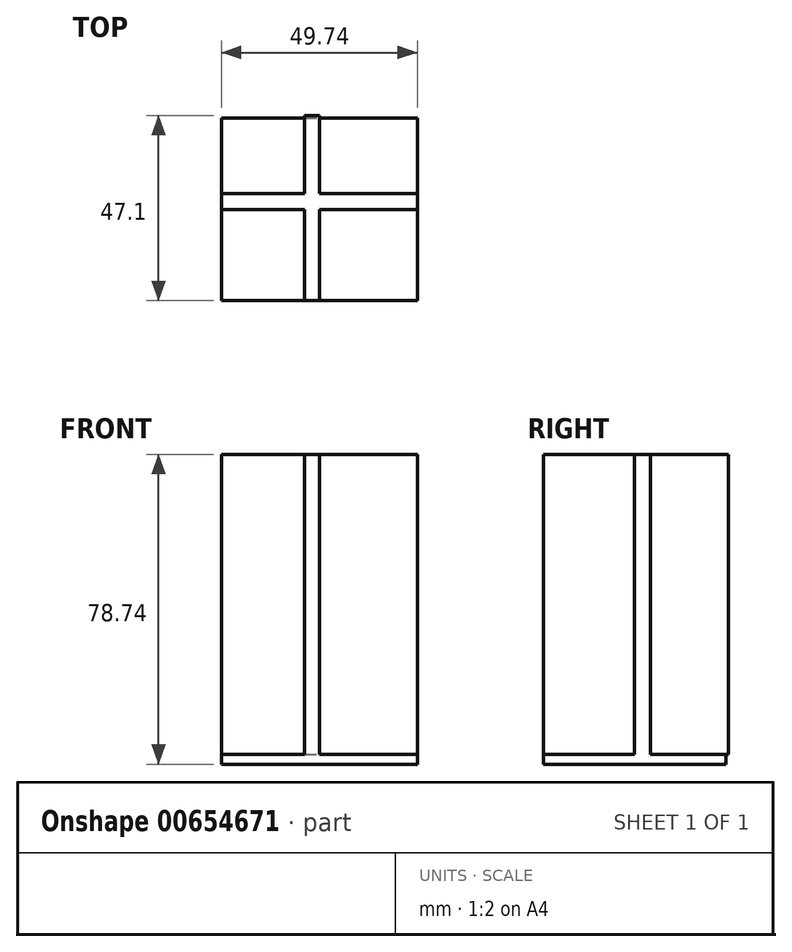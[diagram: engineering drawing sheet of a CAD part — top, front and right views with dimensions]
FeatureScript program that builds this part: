
annotation { "Feature Type Name" : "Feature", "Feature Type Description" : "" }
export const myFeature = defineFeature(function(context is Context, id is Id, definition is map)
    precondition{}
    {
        {
            var Q0;
            Q0=qCreatedBy(makeId("Top.planeOp"),FACE);
            var sketch = newSketch(context, id + "F0", { "sketchPlane" : qUnion([Q0])});
            skLineSegment(sketch, "E0.bottom", {"start": v(-21.1, 19.08) * mm, "end": v(28.63, 19.08) * mm});
            skLineSegment(sketch, "E0.top", {"start": v(-21.1, -27.28) * mm, "end": v(28.63, -27.28) * mm});
            skLineSegment(sketch, "E0.left", {"start": v(-21.1, 19.08) * mm, "end": v(-21.1, -27.28) * mm});
            skLineSegment(sketch, "E0.right", {"start": v(28.63, 19.08) * mm, "end": v(28.63, -27.28) * mm});
            skSolve(sketch);
        }
        {
            var Q0;
            Q0=makeQuery(id+"F0.imprint","IMPRINT",FACE,{"disambiguationData":[TD([[makeQuery(id+"F0.imprint","IMPRINT",EDGE,{"derivedFrom":sQuery(id+"F0.wireOp",EDGE,"E0.bottom")}),-1.0]])]});
            extrude(context, id + "F1", {"entities" : qUnion([Q0]), "depth" : 2.54 * mm, "offsetDistance" : 25.4 * mm});
        }
        {
            var Q0;
            Q0=makeQuery(id+"F1.opExtrude","CAP_FACE",FACE,{"disambiguationData":[OSD([sQuery(id+"F0.wireOp",EDGE,"E0.bottom"),sQuery(id+"F0.wireOp",EDGE,"E0.top"),sQuery(id+"F0.wireOp",EDGE,"E0.left"),sQuery(id+"F0.wireOp",EDGE,"E0.right")])],"isStart":false});
            var sketch = newSketch(context, id + "F2", { "sketchPlane" : qUnion([Q0])});
            skLineSegment(sketch, "E1.bottom", {"start": v(-21.1, -4.1) * mm, "end": v(28.63, -4.1) * mm});
            skLineSegment(sketch, "E1.top", {"start": v(-21.1, 0) * mm, "end": v(28.63, 0) * mm});
            skLineSegment(sketch, "E1.left", {"start": v(-21.1, -4.1) * mm, "end": v(-21.1, 0) * mm});
            skLineSegment(sketch, "E1.right", {"start": v(28.63, -4.1) * mm, "end": v(28.63, 0) * mm});
            skSolve(sketch);
        }
        {
            var Q0;
            Q0=makeQuery(id+"F2.imprint","IMPRINT",FACE,{"disambiguationData":[TD([[makeQuery(id+"F2.imprint","IMPRINT",EDGE,{"derivedFrom":sQuery(id+"F2.wireOp",EDGE,"E1.bottom")}),1.0]])]});
            extrude(context, id + "F3", {"entities" : qUnion([Q0]), "operationType" : NewBodyOperationType.ADD, "depth" : 76.2 * mm, "offsetDistance" : 25.4 * mm});
        }
        {
            var Q0;
            {var subQ0=sQuery(id+"F0.wireOp",EDGE,"E0.right");var subQ1=sQuery(id+"F0.wireOp",EDGE,"E0.left");var subQ2=sQuery(id+"F0.wireOp",EDGE,"E0.top");Q0=makeQuery(id+"F3.boolean.opBoolean","SPLIT",FACE,{"disambiguationData":[TD([makeQuery(id+"F1.opExtrude","SWEPT_FACE",FACE,{"disambiguationData":[OSD([subQ2])]})])],"derivedFrom":makeQuery(id+"F1.opExtrude","CAP_FACE",FACE,{"disambiguationData":[OSD([sQuery(id+"F0.wireOp",EDGE,"E0.bottom"),subQ2,subQ1,subQ0])],"isStart":false})});}
            var sketch = newSketch(context, id + "F4", { "sketchPlane" : qUnion([Q0])});
            skPoint(sketch, "E2.firstSnap0", {"position": v(3.76, -27.28) * mm});
            skPoint(sketch, "E2.oppositeSnap0", {"position": v(3.76, -4.1) * mm});
            skLineSegment(sketch, "E2.bottom", {"start": v(0, -27.28) * mm, "end": v(3.76, -27.28) * mm});
            skLineSegment(sketch, "E2.top", {"start": v(0, 19.82) * mm, "end": v(3.76, 19.82) * mm});
            skLineSegment(sketch, "E2.left", {"start": v(0, -27.28) * mm, "end": v(0, 19.82) * mm});
            skLineSegment(sketch, "E2.right", {"start": v(3.76, -27.28) * mm, "end": v(3.76, 19.82) * mm});
            skSolve(sketch);
        }
        {
            var Q0;
            {var subQ0=sQuery(id+"F4.wireOp",EDGE,"E2.bottom");Q0=makeQuery(id+"F4.imprint","IMPRINT",FACE,{"disambiguationData":[TD([[makeQuery(id+"F4.imprint","IMPRINT",EDGE,{"derivedFrom":subQ0}),1.0]])]});}
            var Q1;
            {var subQ0=sQuery(id+"F4.wireOp",EDGE,"E2.top");Q1=makeQuery(id+"F4.imprint","IMPRINT",FACE,{"disambiguationData":[TD([[makeQuery(id+"F4.imprint","IMPRINT",EDGE,{"derivedFrom":subQ0}),-1.0]])]});}
            extrude(context, id + "F5", {"entities" : qUnion([Q0, Q1]), "operationType" : NewBodyOperationType.ADD, "depth" : 76.2 * mm, "offsetDistance" : 25.4 * mm});
        }
        {
            var Q0;
            {var subQ2=sQuery(id+"F0.wireOp",EDGE,"E0.left");var subQ3=makeQuery(id+"F1.opExtrude","SWEPT_FACE",FACE,{"disambiguationData":[OSD([subQ2])]});var subQ4=sQuery(id+"F0.wireOp",EDGE,"E0.bottom");var subQ5=makeQuery(id+"F1.opExtrude","SWEPT_FACE",FACE,{"disambiguationData":[OSD([subQ4])]});var subQ7=sQuery(id+"F0.wireOp",EDGE,"E0.right");Q0=makeQuery(id+"F5.boolean.opBoolean","SPLIT",FACE,{"disambiguationData":[TD([subQ3])],"derivedFrom":makeQuery(id+"F3.boolean.opBoolean","SPLIT",FACE,{"disambiguationData":[TD([subQ5])],"derivedFrom":makeQuery(id+"F1.opExtrude","CAP_FACE",FACE,{"disambiguationData":[OSD([subQ4,sQuery(id+"F0.wireOp",EDGE,"E0.top"),subQ2,subQ7])],"isStart":false})})});}
            var sketch = newSketch(context, id + "F6", { "sketchPlane" : qUnion([Q0])});
            skLineSegment(sketch, "E3.bottom", {"start": v(-21.1, 19.08) * mm, "end": v(28.22, 19.08) * mm});
            skLineSegment(sketch, "E3.top", {"start": v(-21.1, 19.08) * mm, "end": v(28.22, 19.08) * mm});
            skLineSegment(sketch, "E3.left", {"start": v(-21.1, 19.08) * mm, "end": v(-21.1, 19.08) * mm});
            skLineSegment(sketch, "E3.right", {"start": v(28.22, 19.08) * mm, "end": v(28.22, 19.08) * mm});
            skLineSegment(sketch, "E4.top", {"start": v(28.22, -26.09) * mm, "end": v(28.22, -26.09) * mm});
            skLineSegment(sketch, "E4.left", {"start": v(28.22, 19.08) * mm, "end": v(28.22, -26.09) * mm});
            skLineSegment(sketch, "E4.right", {"start": v(28.22, 19.08) * mm, "end": v(28.22, -26.09) * mm});
            skLineSegment(sketch, "E5.bottom", {"start": v(28.22, -26.09) * mm, "end": v(-21.1, -26.09) * mm});
            skLineSegment(sketch, "E5.top", {"start": v(28.22, -26.09) * mm, "end": v(-21.1, -26.09) * mm});
            skLineSegment(sketch, "E5.right", {"start": v(-21.1, -26.09) * mm, "end": v(-21.1, -26.09) * mm});
            skLineSegment(sketch, "E6.left", {"start": v(-21.1, -26.09) * mm, "end": v(-21.1, 19.08) * mm});
            skLineSegment(sketch, "E6.right", {"start": v(-21.1, -26.09) * mm, "end": v(-21.1, 19.08) * mm});
            skSolve(sketch);
        }
        {
            var Q0;
            Q0=sQuery(id+"F6.wireOp",EDGE,"E3.top");
            var Q1;
            Q1=sQuery(id+"F6.wireOp",EDGE,"E6.right");
            var Q2;
            Q2=sQuery(id+"F6.wireOp",EDGE,"E5.top");
            var Q3;
            Q3=sQuery(id+"F6.wireOp",EDGE,"E4.right");
            extrude(context, id + "F7", {"bodyType" : ToolBodyType.SURFACE, "surfaceEntities" : qUnion([Q0, Q1, Q2, Q3]), "depth" : 76.2 * mm, "offsetDistance" : 25.4 * mm});
        }
    });
